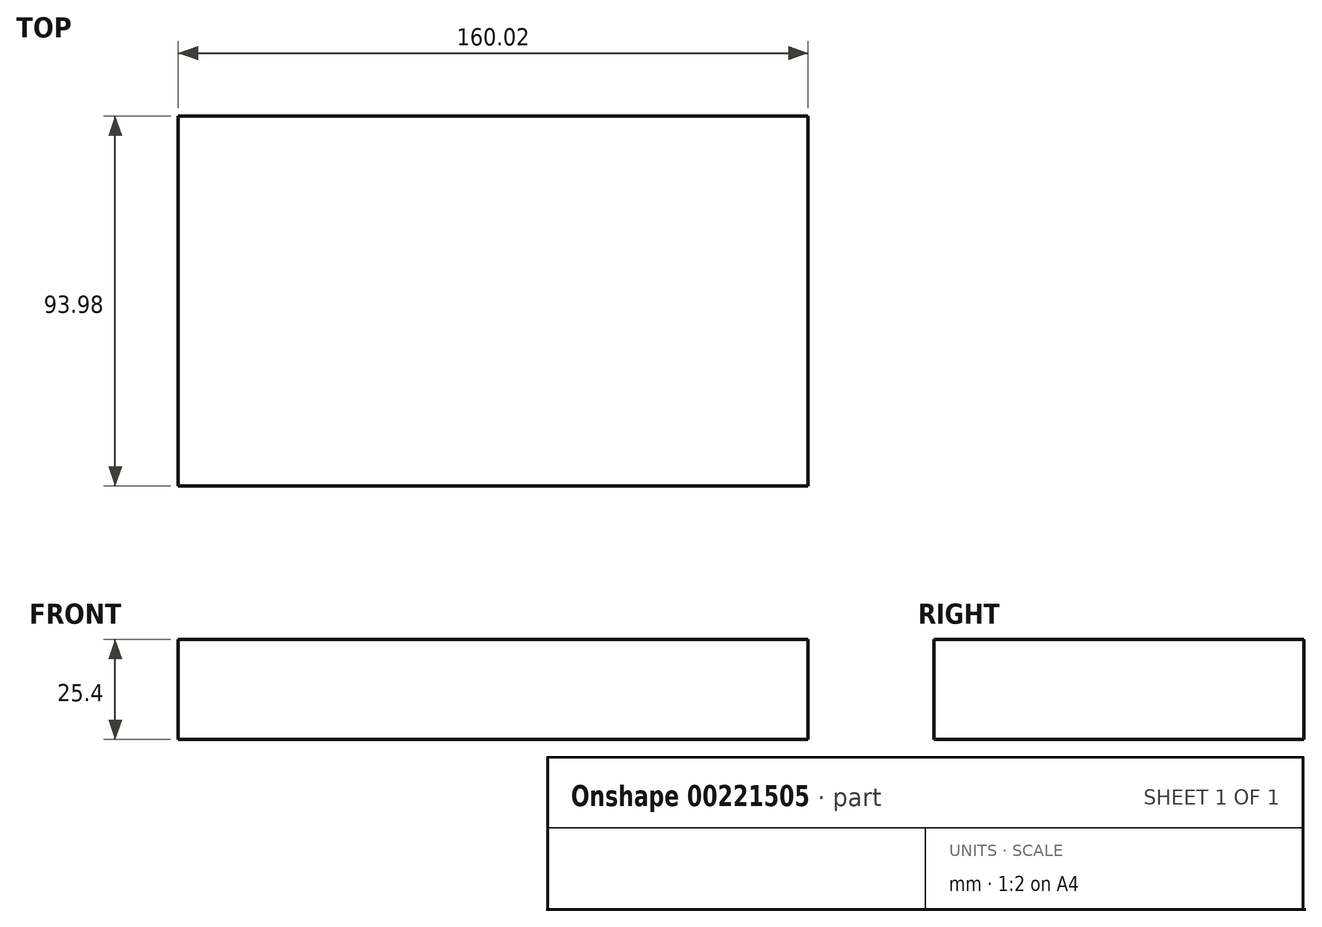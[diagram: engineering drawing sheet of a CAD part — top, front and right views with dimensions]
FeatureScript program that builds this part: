
annotation { "Feature Type Name" : "Feature", "Feature Type Description" : "" }
export const myFeature = defineFeature(function(context is Context, id is Id, definition is map)
    precondition{}
    {
        {
            var Q0;
            Q0=qCreatedBy(makeId("Top.planeOp"),FACE);
            var sketch = newSketch(context, id + "F0", { "sketchPlane" : qUnion([Q0])});
            skLineSegment(sketch, "E0.bottom", {"start": v(80, 47) * mm, "end": v(-80.01, 47) * mm});
            skLineSegment(sketch, "E0.top", {"start": v(80.01, -47) * mm, "end": v(-80.01, -47) * mm});
            skLineSegment(sketch, "E0.left", {"start": v(80.01, 47) * mm, "end": v(80.01, -47) * mm});
            skLineSegment(sketch, "E0.right", {"start": v(-80.01, 47) * mm, "end": v(-80.01, -47) * mm});
            skPoint(sketch, "E0.middle", {"position": v(0, 0) * mm});
            skSolve(sketch);
        }
        {
            var Q0;
            Q0=makeQuery(id+"F0.imprint","IMPRINT",FACE,{"disambiguationData":[TD([[makeQuery(id+"F0.imprint","IMPRINT",EDGE,{"derivedFrom":sQuery(id+"F0.wireOp",EDGE,"E0.bottom")}),1.0]])]});
            extrude(context, id + "F1", {"entities" : qUnion([Q0]), "depth" : 25.4 * mm});
        }
    });
